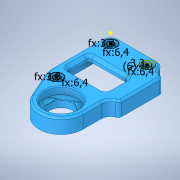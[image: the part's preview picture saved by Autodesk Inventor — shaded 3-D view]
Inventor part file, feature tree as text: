
AUTODESK INVENTOR PART (.ipt)
format: ipt  version: 2021.1 (Build 251245010, 245A)  size: 311,808 bytes
history: mixed  units: in
note: dims shown in document units (in); Inventor stores cm internally (conversion verified against a paired STEP export)
features: move_body x3, extrude x2, direct_edit x1, sketch x1, imported_body x1
ambient origin geometry x8: Origin, YZ Plane, XZ Plane, XY Plane, X Axis, Y Axis, Z Axis, Center Point
bodies: Solid1 (imported_parasolid), Body2 (imported_parasolid)
feature tree (8):
  direct_edit  "Direktbearbeitung1"
  sketch  "Skizze1"  dims[d0=0.0in d1=0.0in d2=-0.0138in d3=0.0in d4=0.0in d5=-0.0138in d6=0.0in d7=0.0in d8=-0.0138in d9=0.1299in d10=0.1299in d11=0.1299in d12=0.3937in d13=0.0in d14=0.2362in d15=0.252in d16=0.252in d17=0.252in d18=0.3937in d19=0.0in]
  extrude  "Extrusion1"  TaperAngle=0.0deg  [1 undecoded]
  extrude  "Extrusion2"  TaperAngle=0.0deg  [1 undecoded]
  move_body  "Verschieben1"
  move_body  "Verschieben2"
  move_body  "Verschieben3"
  imported_body  NMx_Import_Brep_tag  [imported B-rep: ~157 faces, bbox_mm=[34.6, 8.0, 53.550254]]
note: 2 required parameter values undecoded (feature->parameter linkage not recoverable at this tier; creation-order binding heuristic only, values carry confidence <= 0.55)
